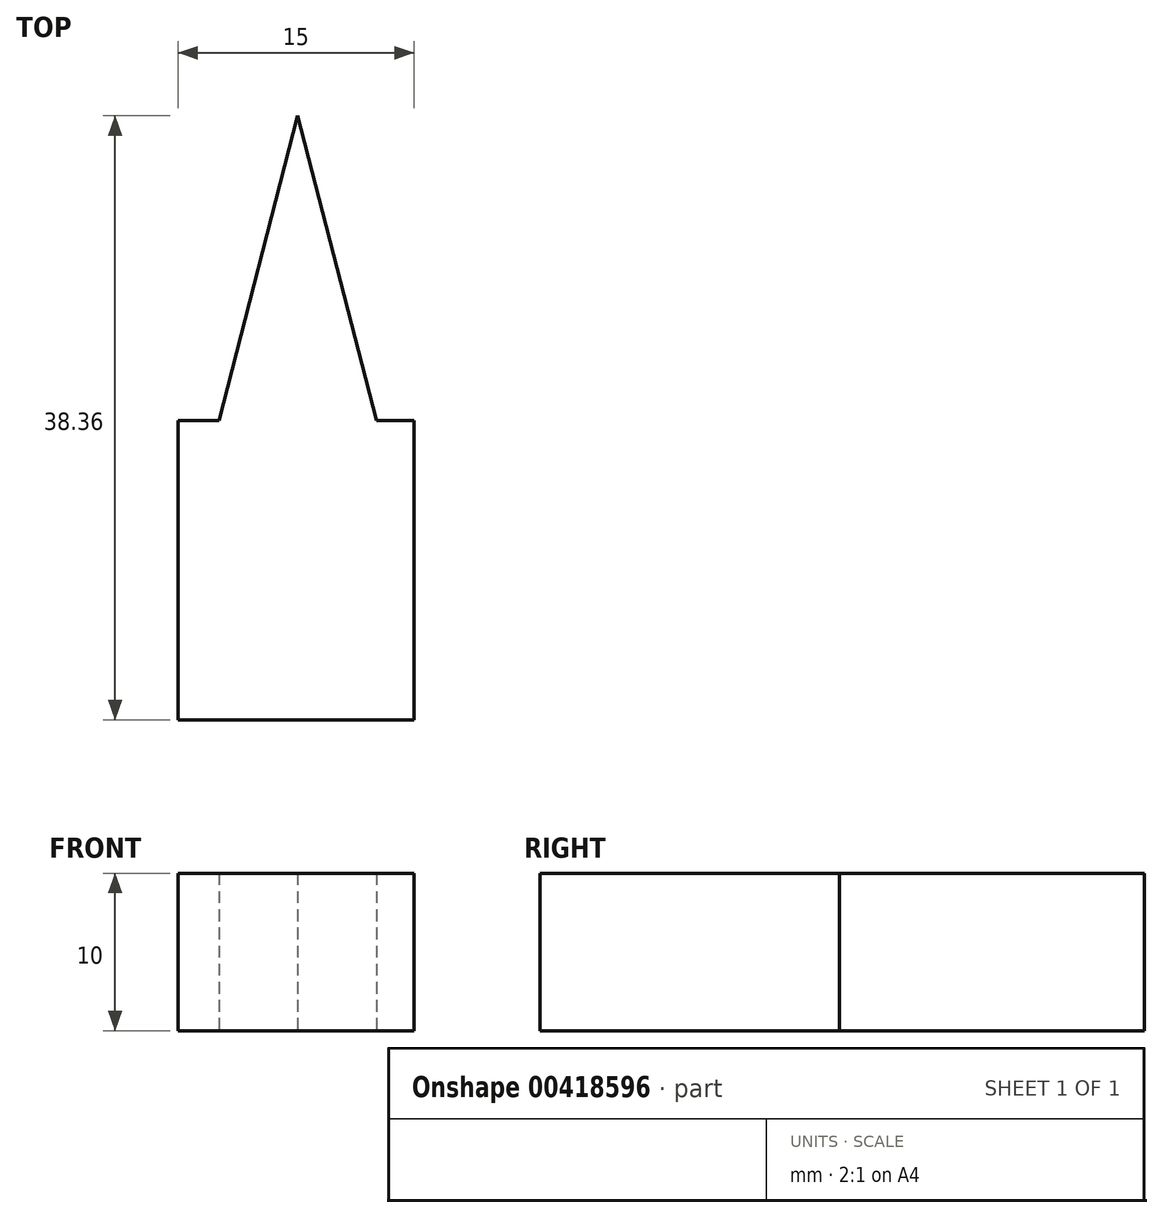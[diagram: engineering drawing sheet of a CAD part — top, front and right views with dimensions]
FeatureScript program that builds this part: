
annotation { "Feature Type Name" : "Feature", "Feature Type Description" : "" }
export const myFeature = defineFeature(function(context is Context, id is Id, definition is map)
    precondition{}
    {
        {
            var Q0;
            Q0=qCreatedBy(makeId("Top.planeOp"),FACE);
            var sketch = newSketch(context, id + "F0", { "sketchPlane" : qUnion([Q0])});
            skLineSegment(sketch, "E0", {"start": v(-62.35, 0) * mm, "end": v(-57.35, 19.36) * mm});
            skLineSegment(sketch, "E1", {"start": v(-57.35, 19.36) * mm, "end": v(-52.35, 0) * mm});
            skLineSegment(sketch, "E2", {"start": v(-62.35, 0) * mm, "end": v(-52.35, 0) * mm});
            skLineSegment(sketch, "E3.bottom", {"start": v(-64.95, 0) * mm, "end": v(-49.95, 0) * mm});
            skLineSegment(sketch, "E3.top", {"start": v(-64.95, -19) * mm, "end": v(-49.95, -19) * mm});
            skLineSegment(sketch, "E3.left", {"start": v(-64.95, 0) * mm, "end": v(-64.95, -19) * mm});
            skLineSegment(sketch, "E3.right", {"start": v(-49.95, 0) * mm, "end": v(-49.95, -19) * mm});
            skSolve(sketch);
        }
        {
            var Q0;
            {var subQ0=sQuery(id+"F0.wireOp",EDGE,"E0");Q0=makeQuery(id+"F0.imprint","IMPRINT",FACE,{"disambiguationData":[TD([[makeQuery(id+"F0.imprint","IMPRINT",EDGE,{"derivedFrom":subQ0}),-1.0]])]});}
            var Q1;
            Q1=makeQuery(id+"F0.imprint","IMPRINT",FACE,{"disambiguationData":[TD([[makeQuery(id+"F0.imprint","IMPRINT",EDGE,{"derivedFrom":sQuery(id+"F0.wireOp",EDGE,"E3.top")}),1.0]])]});
            extrude(context, id + "F1", {"entities" : qUnion([Q0, Q1]), "endBound" : BoundingType.SYMMETRIC, "depth" : 10 * mm});
        }
    });
